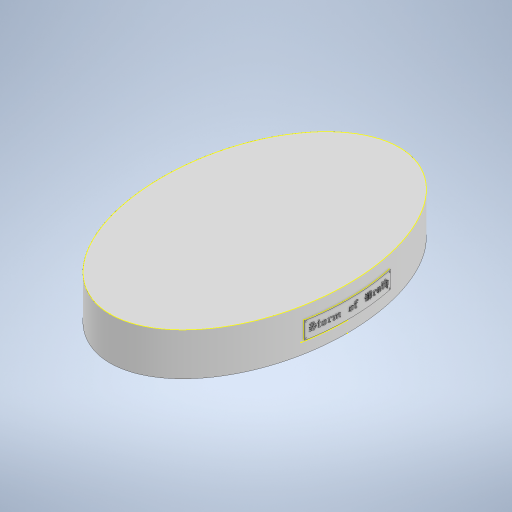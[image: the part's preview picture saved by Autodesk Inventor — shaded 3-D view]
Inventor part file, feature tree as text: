
AUTODESK INVENTOR PART (.ipt)
format: ipt  version: 2024 (Build 280153000, 153)  size: 3,841,536 bytes
history: native  units: mm
features: split x27, thicken_offset x17, sketch x4, extrude x2, plane x1, fillet x1, other x1
ambient origin geometry x8: Origin, YZ Plane, XZ Plane, XY Plane, X Axis, Y Axis, Z Axis, Center Point
bodies: Solid1 (feature_tree)
feature tree (53):
  extrude  "Extrusion1"  Depth=54.5mm
  extrude  "Extrusion2"  Depth=51.0mm
  plane  "Work Plane2"
  sketch  "Sketch4"  dims[d6=3.0mm d7=0.0mm d9=80.0mm d10=32.748225mm d14=10.0mm d16=51.0mm d19=0.75mm d20=0.75mm d21=0.75mm d22=0.75mm d23=0.75mm d25=0.75mm d26=0.75mm d27=0.75mm d28=0.75mm d70=0.75mm d71=0.75mm d72=0.5mm d73=0.5mm d74=0.5mm d75=0.5mm d76=0.5mm d77=0.5mm d78=0.5mm d79=0.5mm d80=0.5mm d81=0.5mm d82=0.5mm d83=0.5mm d84=0.5mm d85=0.5mm d86=0.5mm d87=0.5mm d88=0.5mm d89=0.5mm d90=0.5mm d91=0.5mm d92=0.5mm d93=0.5mm d94=0.5mm d95=0.5mm d96=0.4mm d97=0.4mm d98=0.4mm d99=0.4mm d100=0.4mm d101=0.4mm d102=0.4mm d103=0.4mm d104=0.35mm]
  sketch  "3D Sketch2"
  split  "Split28"
  split  "Split29"
  split  "Split30"
  split  "Split31"
  split  "Split32"
  split  "Split33"
  split  "Split34"
  split  "Split35"
  split  "Split36"
  split  "Split37"
  split  "Split38"
  split  "Split39"
  split  "Split40"
  split  "Split41"
  split  "Split42"
  split  "Split43"
  split  "Split44"
  split  "Split45"
  split  "Split46"
  split  "Split47"
  split  "Split48"
  split  "Split49"
  split  "Split50"
  split  "Split51"
  split  "Split52"
  split  "Split53"
  split  "Split54"
  thicken_offset  "Thicken20"
  thicken_offset  "Thicken21"
  thicken_offset  "Thicken22"
  thicken_offset  "Thicken23"
  thicken_offset  "Thicken24"
  thicken_offset  "Thicken25"
  thicken_offset  "Thicken26"
  thicken_offset  "Thicken27"
  thicken_offset  "Thicken28"
  thicken_offset  "Thicken29"
  thicken_offset  "Thicken30"
  thicken_offset  "Thicken31"
  thicken_offset  "Thicken32"
  thicken_offset  "Thicken33"
  thicken_offset  "Thicken34"
  thicken_offset  "Thicken35"
  thicken_offset  "Thicken36"
  fillet  "Fillet2"  Radius=22.0mm
  sketch  "Sketch1"  dims[d0=85.0mm d1=54.5mm]
  sketch  "Sketch2"  dims[d2=81.5mm d3=51.0mm d4=22.0mm d5=0.0mm]
  other  "Project to Surface2"
